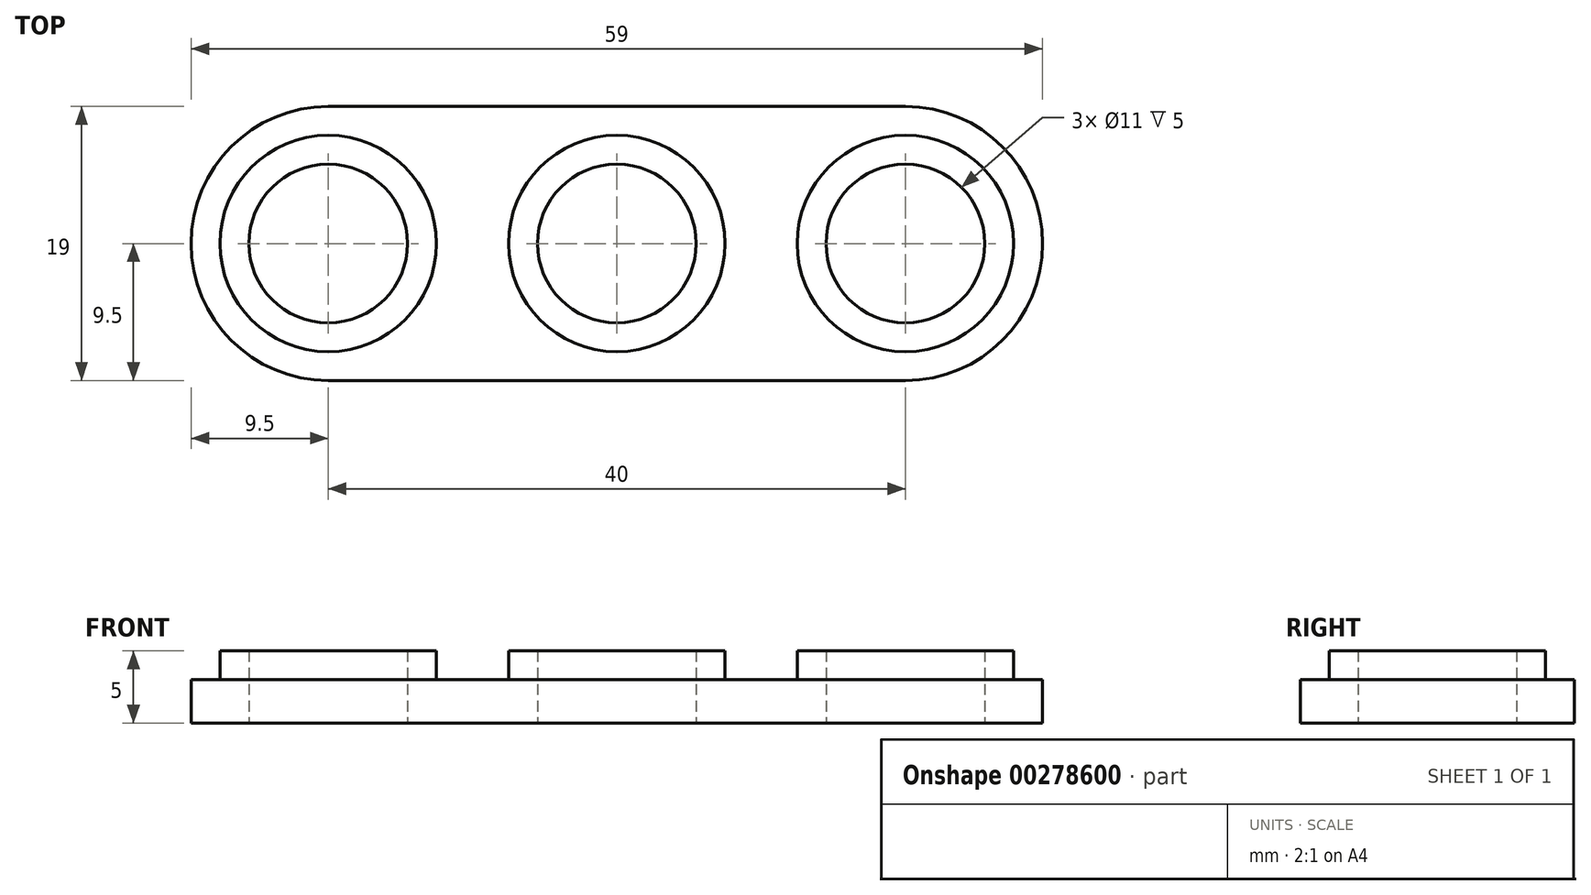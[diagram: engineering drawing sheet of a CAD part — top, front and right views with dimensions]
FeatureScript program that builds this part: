
annotation { "Feature Type Name" : "Feature", "Feature Type Description" : "" }
export const myFeature = defineFeature(function(context is Context, id is Id, definition is map)
    precondition{}
    {
        {
            assignVariable(context, id + "F0", {"name" : "e", "anyValue" : 3});
        }
        {
            assignVariable(context, id + "F1", {"name" : "h0", "anyValue" : 2});
        }
        {
            var Q0;
            Q0=qCreatedBy(makeId("Top.planeOp"),FACE);
            var sketch = newSketch(context, id + "F2", { "sketchPlane" : qUnion([Q0])});
            skLineSegment(sketch, "E0.bottom", {"start": v(0, 9.5) * mm, "end": v(40, 9.5) * mm});
            skLineSegment(sketch, "E0.top", {"start": v(0, -9.5) * mm, "end": v(40, -9.5) * mm});
            skLineSegment(sketch, "E0.left", {"start": v(-9.5, 0) * mm, "end": v(-9.5, 0) * mm});
            skLineSegment(sketch, "E0.right", {"start": v(49.5, 0) * mm, "end": v(49.5, 0) * mm});
            skPoint(sketch, "E1", {"position": v(-9.5, 0) * mm});
            skCircle(sketch, "E2", {"center": v(0, 0) * mm, "radius": 5.5 * mm});
            skPoint(sketch, "E3.visualSharp", {"position": v(49.5, 9.5) * mm});
            skArc(sketch, "E3.filletArc", {"start": v(49.5, 0) * mm, "mid": v(46.72, 6.72) * mm, "end": v(40, 9.5) * mm});
            skPoint(sketch, "E4.visualSharp", {"position": v(49.5, -9.5) * mm});
            skArc(sketch, "E4.filletArc", {"start": v(40, -9.5) * mm, "mid": v(46.72, -6.72) * mm, "end": v(49.5, 0) * mm});
            skPoint(sketch, "E5.visualSharp", {"position": v(-9.5, -9.5) * mm});
            skArc(sketch, "E5.filletArc", {"start": v(-9.5, 0) * mm, "mid": v(-6.72, -6.72) * mm, "end": v(0, -9.5) * mm});
            skPoint(sketch, "E6.visualSharp", {"position": v(-9.5, 9.5) * mm});
            skArc(sketch, "E6.filletArc", {"start": v(0, 9.5) * mm, "mid": v(-6.72, 6.72) * mm, "end": v(-9.5, 0) * mm});
            skCircle(sketch, "E7", {"center": v(0, 0) * mm, "radius": 7.5 * mm});
            skCircle(sketch, "E8.1.0.0", {"center": v(20, 0) * mm, "radius": 5.5 * mm});
            skCircle(sketch, "E8.1.0.1", {"center": v(20, 0) * mm, "radius": 7.5 * mm});
            skCircle(sketch, "E8.2.0.0", {"center": v(40, 0) * mm, "radius": 5.5 * mm});
            skCircle(sketch, "E8.2.0.1", {"center": v(40, 0) * mm, "radius": 7.5 * mm});
            skLineSegment(sketch, "E8.direction1", {"start": v(0, 0) * mm, "end": v(20, 0) * mm, "construction": true});
            skSolve(sketch);
        }
        {
            var Q0;
            Q0=qSketchRegion(id+"F2",true);
            var Q1;
            Q1=makeQuery(id+"F2.imprint","IMPRINT",FACE,{"disambiguationData":[TD([[makeQuery(id+"F2.imprint","IMPRINT",EDGE,{"derivedFrom":sQuery(id+"F2.wireOp",EDGE,"E2")}),-1.0]])]});
            var Q2;
            Q2=makeQuery(id+"F2.imprint","IMPRINT",FACE,{"disambiguationData":[TD([[makeQuery(id+"F2.imprint","IMPRINT",EDGE,{"derivedFrom":sQuery(id+"F2.wireOp",EDGE,"E8.1.0.0")}),-1.0]])]});
            var Q3;
            Q3=makeQuery(id+"F2.imprint","IMPRINT",FACE,{"disambiguationData":[TD([[makeQuery(id+"F2.imprint","IMPRINT",EDGE,{"derivedFrom":sQuery(id+"F2.wireOp",EDGE,"E8.2.0.0")}),-1.0]])]});
            var Q4;
            Q4=makeQuery(id+"F2.imprint","IMPRINT",FACE,{"disambiguationData":[TD([[makeQuery(id+"F2.imprint","IMPRINT",EDGE,{"derivedFrom":sQuery(id+"F2.wireOp",EDGE,"345b2114-0edb-480d-a68f-e22b198684d9.0.3.0")}),-1.0]])]});
            extrude(context, id + "F3", {"entities" : qUnion([Q0, Q1, Q2, Q3, Q4]), "depth" : (getVariable(context, 'e')) * mm});
        }
        {
            var Q0;
            Q0=makeQuery(id+"F2.imprint","IMPRINT",FACE,{"disambiguationData":[TD([[makeQuery(id+"F2.imprint","IMPRINT",EDGE,{"derivedFrom":sQuery(id+"F2.wireOp",EDGE,"E2")}),-1.0]])]});
            var Q1;
            Q1=makeQuery(id+"F2.imprint","IMPRINT",FACE,{"disambiguationData":[TD([[makeQuery(id+"F2.imprint","IMPRINT",EDGE,{"derivedFrom":sQuery(id+"F2.wireOp",EDGE,"E8.1.0.0")}),-1.0]])]});
            var Q2;
            Q2=makeQuery(id+"F2.imprint","IMPRINT",FACE,{"disambiguationData":[TD([[makeQuery(id+"F2.imprint","IMPRINT",EDGE,{"derivedFrom":sQuery(id+"F2.wireOp",EDGE,"E8.2.0.0")}),-1.0]])]});
            var Q3;
            Q3=makeQuery(id+"F2.imprint","IMPRINT",FACE,{"disambiguationData":[TD([[makeQuery(id+"F2.imprint","IMPRINT",EDGE,{"derivedFrom":sQuery(id+"F2.wireOp",EDGE,"345b2114-0edb-480d-a68f-e22b198684d9.0.3.0")}),-1.0]])]});
            extrude(context, id + "F4", {"entities" : qUnion([Q0, Q1, Q2, Q3]), "operationType" : NewBodyOperationType.ADD, "depth" : (getVariable(context, 'e') + getVariable(context, 'h0')) * mm});
        }
    });
